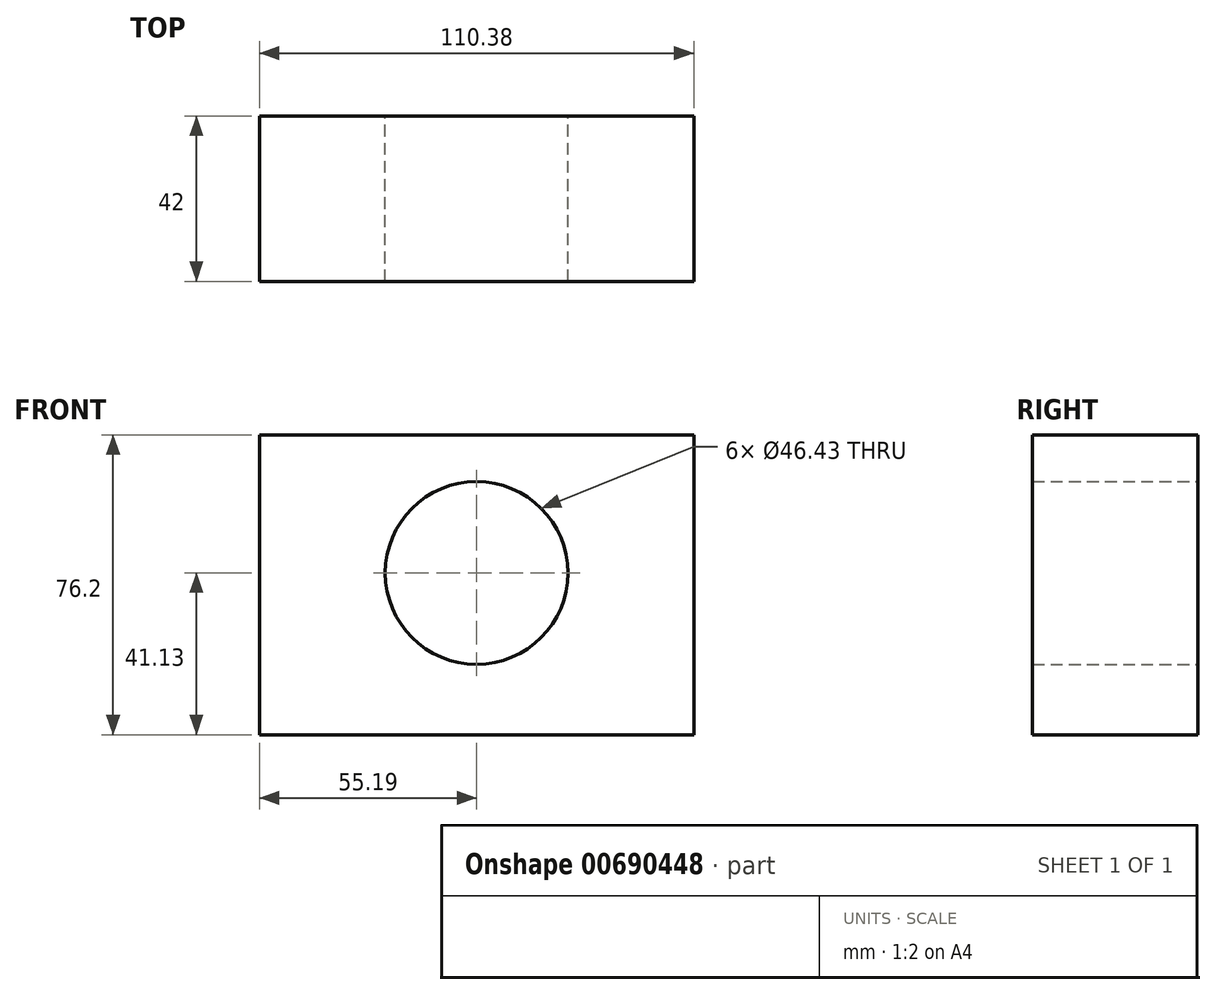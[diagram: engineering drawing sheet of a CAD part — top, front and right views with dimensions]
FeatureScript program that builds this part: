
annotation { "Feature Type Name" : "Feature", "Feature Type Description" : "" }
export const myFeature = defineFeature(function(context is Context, id is Id, definition is map)
    precondition{}
    {
        {
            var Q0;
            Q0=qCreatedBy(makeId("Front.planeOp"),FACE);
            var sketch = newSketch(context, id + "F0", { "sketchPlane" : qUnion([Q0])});
            skLineSegment(sketch, "E0.bottom", {"start": v(-55.2, 35.07) * mm, "end": v(55.2, 35.07) * mm});
            skLineSegment(sketch, "E0.top", {"start": v(-55.2, -41.13) * mm, "end": v(55.2, -41.13) * mm});
            skLineSegment(sketch, "E0.left", {"start": v(-55.2, 35.07) * mm, "end": v(-55.2, -41.13) * mm});
            skLineSegment(sketch, "E0.right", {"start": v(55.2, 35.07) * mm, "end": v(55.2, -41.13) * mm});
            skPoint(sketch, "E0.middle", {"position": v(0, -3.03) * mm});
            skCircle(sketch, "E1", {"center": v(0, 0) * mm, "radius": 23.21 * mm});
            skSolve(sketch);
        }
        {
            var Q0;
            Q0=makeQuery(id+"F0.imprint","IMPRINT",FACE,{"disambiguationData":[TD([[makeQuery(id+"F0.imprint","IMPRINT",EDGE,{"derivedFrom":sQuery(id+"F0.wireOp",EDGE,"E0.bottom")}),-1.0]])]});
            extrude(context, id + "F1", {"entities" : qUnion([Q0]), "depth" : 42 * mm, "offsetDistance" : 25.4 * mm});
        }
    });
